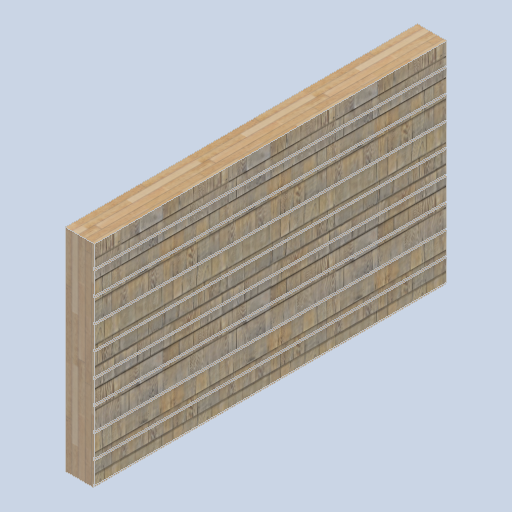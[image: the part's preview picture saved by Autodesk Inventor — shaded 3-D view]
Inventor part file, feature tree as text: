
AUTODESK INVENTOR PART (.ipt)
format: ipt  version: 2024.2 (Build 282272000, 272)  size: 371,712 bytes
history: native  units: in
note: dims shown in document units (in); Inventor stores cm internally (conversion verified against a paired STEP export)
features: other x3, sketch x2
ambient origin geometry x8: Origin, YZ Plane, XZ Plane, XY Plane, X Axis, Y Axis, Z Axis, Center Point
bodies: Solid1 (feature_tree)
feature tree (5):
  other  "side_wall_block_02_MIR.ipt"
  other  "Solid1::side_wall_block_02_MIR.ipt"
  other  "TaggingFeature1"
  sketch  "Sketch1"  dims[d0=0.3937in]
  sketch  "Sketch2"
